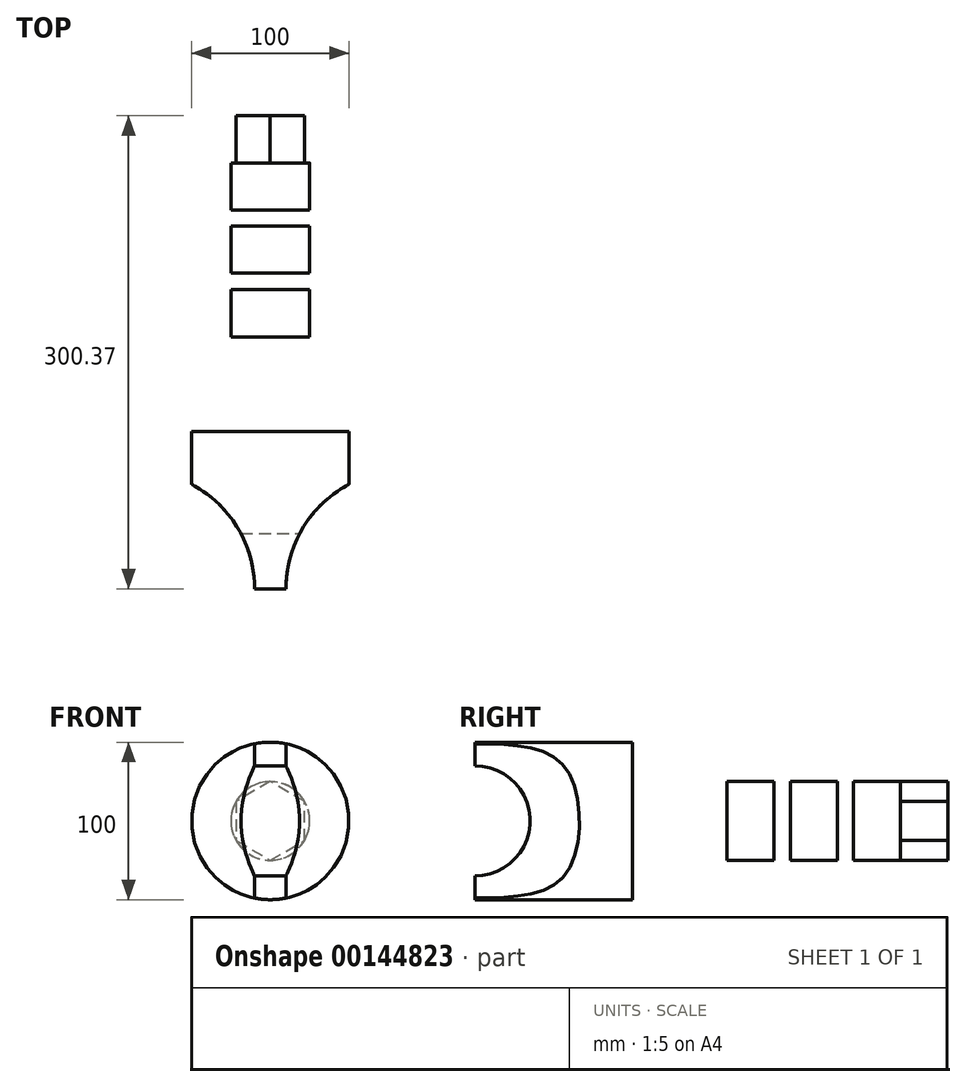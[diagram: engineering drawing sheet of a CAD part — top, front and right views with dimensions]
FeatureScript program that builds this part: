
annotation { "Feature Type Name" : "Feature", "Feature Type Description" : "" }
export const myFeature = defineFeature(function(context is Context, id is Id, definition is map)
    precondition{}
    {
        {
            var Q0;
            Q0=qCreatedBy(makeId("Top.planeOp"),FACE);
            var sketch = newSketch(context, id + "F0", { "sketchPlane" : qUnion([Q0])});
            skLineSegment(sketch, "E0", {"start": v(0, 0) * mm, "end": v(0, 300) * mm});
            skLineSegment(sketch, "E1.bottom", {"start": v(0, 0) * mm, "end": v(-50, 0) * mm});
            skLineSegment(sketch, "E1.top", {"start": v(0, 100) * mm, "end": v(-50, 100) * mm});
            skLineSegment(sketch, "E1.left", {"start": v(0, 0) * mm, "end": v(0, 100) * mm});
            skLineSegment(sketch, "E1.right", {"start": v(-50, 0) * mm, "end": v(-50, 100) * mm});
            skLineSegment(sketch, "E2.bottom", {"start": v(0, 100) * mm, "end": v(-25, 100) * mm});
            skLineSegment(sketch, "E2.top", {"start": v(0, 150) * mm, "end": v(-25, 150) * mm});
            skLineSegment(sketch, "E2.left", {"start": v(0, 100) * mm, "end": v(0, 150) * mm});
            skLineSegment(sketch, "E2.right", {"start": v(-25, 100) * mm, "end": v(-25, 150) * mm});
            skLineSegment(sketch, "E3.bottom", {"start": v(-12.5, 150) * mm, "end": v(0, 150) * mm});
            skLineSegment(sketch, "E3.top", {"start": v(-12.5, 160) * mm, "end": v(0, 160) * mm});
            skLineSegment(sketch, "E3.left", {"start": v(-12.5, 150) * mm, "end": v(-12.5, 160) * mm});
            skLineSegment(sketch, "E3.right", {"start": v(0, 150) * mm, "end": v(0, 160) * mm});
            skLineSegment(sketch, "E4.bottom", {"start": v(-25, 160) * mm, "end": v(0, 160) * mm});
            skLineSegment(sketch, "E4.top", {"start": v(-25, 190) * mm, "end": v(0, 190) * mm});
            skLineSegment(sketch, "E4.left", {"start": v(-25, 160) * mm, "end": v(-25, 190) * mm});
            skLineSegment(sketch, "E4.right", {"start": v(0, 160) * mm, "end": v(0, 190) * mm});
            skLineSegment(sketch, "E5.bottom", {"start": v(-12.5, 190) * mm, "end": v(0, 190) * mm});
            skLineSegment(sketch, "E5.top", {"start": v(-12.5, 200.37) * mm, "end": v(0, 200.37) * mm});
            skLineSegment(sketch, "E5.left", {"start": v(-12.5, 190) * mm, "end": v(-12.5, 200.37) * mm});
            skLineSegment(sketch, "E5.right", {"start": v(0, 190) * mm, "end": v(0, 200.37) * mm});
            skLineSegment(sketch, "E6.bottom", {"start": v(-25, 200.37) * mm, "end": v(0, 200.37) * mm});
            skLineSegment(sketch, "E6.top", {"start": v(-25, 230.37) * mm, "end": v(0, 230.37) * mm});
            skLineSegment(sketch, "E6.left", {"start": v(-25, 200.37) * mm, "end": v(-25, 230.37) * mm});
            skLineSegment(sketch, "E6.right", {"start": v(0, 200.37) * mm, "end": v(0, 230.37) * mm});
            skLineSegment(sketch, "E7.bottom", {"start": v(-12.5, 230.37) * mm, "end": v(0, 230.37) * mm});
            skLineSegment(sketch, "E7.top", {"start": v(-12.5, 240.37) * mm, "end": v(0, 240.37) * mm});
            skLineSegment(sketch, "E7.left", {"start": v(-12.5, 230.37) * mm, "end": v(-12.5, 240.37) * mm});
            skLineSegment(sketch, "E7.right", {"start": v(0, 230.37) * mm, "end": v(0, 240.37) * mm});
            skLineSegment(sketch, "E8.bottom", {"start": v(-25, 240.37) * mm, "end": v(0, 240.37) * mm});
            skLineSegment(sketch, "E8.top", {"start": v(-25, 270.37) * mm, "end": v(0, 270.37) * mm});
            skLineSegment(sketch, "E8.left", {"start": v(-25, 240.37) * mm, "end": v(-25, 270.37) * mm});
            skLineSegment(sketch, "E8.right", {"start": v(0, 240.37) * mm, "end": v(0, 270.37) * mm});
            skSolve(sketch);
        }
        {
            var Q0;
            Q0=makeQuery(id+"F0.imprint","IMPRINT",FACE,{"disambiguationData":[TD([[makeQuery(id+"F0.imprint","IMPRINT",EDGE,{"derivedFrom":sQuery(id+"F0.wireOp",EDGE,"E1.bottom")}),-1.0]])]});
            var Q1;
            Q1=makeQuery(id+"F0.imprint","IMPRINT",FACE,{"disambiguationData":[TD([[makeQuery(id+"F0.imprint","IMPRINT",EDGE,{"derivedFrom":sQuery(id+"F0.wireOp",EDGE,"E2.bottom")}),-1.0]])]});
            var Q2;
            Q2=makeQuery(id+"F0.imprint","IMPRINT",FACE,{"disambiguationData":[TD([[makeQuery(id+"F0.imprint","IMPRINT",EDGE,{"derivedFrom":sQuery(id+"F0.wireOp",EDGE,"E3.bottom")}),1.0]])]});
            var Q3;
            Q3=makeQuery(id+"F0.imprint","IMPRINT",FACE,{"disambiguationData":[TD([[makeQuery(id+"F0.imprint","IMPRINT",EDGE,{"derivedFrom":sQuery(id+"F0.wireOp",EDGE,"E4.top")}),-1.0]])]});
            var Q4;
            Q4=makeQuery(id+"F0.imprint","IMPRINT",FACE,{"disambiguationData":[TD([[makeQuery(id+"F0.imprint","IMPRINT",EDGE,{"derivedFrom":sQuery(id+"F0.wireOp",EDGE,"E5.bottom")}),1.0]])]});
            var Q5;
            Q5=makeQuery(id+"F0.imprint","IMPRINT",FACE,{"disambiguationData":[TD([[makeQuery(id+"F0.imprint","IMPRINT",EDGE,{"derivedFrom":sQuery(id+"F0.wireOp",EDGE,"E6.top")}),-1.0]])]});
            var Q6;
            Q6=makeQuery(id+"F0.imprint","IMPRINT",FACE,{"disambiguationData":[TD([[makeQuery(id+"F0.imprint","IMPRINT",EDGE,{"derivedFrom":sQuery(id+"F0.wireOp",EDGE,"E7.bottom")}),1.0]])]});
            var Q7;
            Q7=makeQuery(id+"F0.imprint","IMPRINT",FACE,{"disambiguationData":[TD([[makeQuery(id+"F0.imprint","IMPRINT",EDGE,{"derivedFrom":sQuery(id+"F0.wireOp",EDGE,"E8.top")}),-1.0]])]});
            var Q8;
            Q8=sQuery(id+"F0.wireOp",EDGE,"E0");
            revolve(context, id + "F1", {"entities" : qUnion([Q0, Q1, Q2, Q3, Q4, Q5, Q6, Q7]), "axis" : qUnion([Q8]), "revolveType" : RevolveType.FULL});
        }
        {
            var Q0;
            Q0=makeQuery(id+"F1.opRevolve","SWEPT_FACE",FACE,{"disambiguationData":[OSD([sQuery(id+"F0.wireOp",EDGE,"E8.top")])]});
            var sketch = newSketch(context, id + "F2", { "sketchPlane" : qUnion([Q0])});
            skCircle(sketch, "E9.cCircle", {"center": v(0, 0) * mm, "radius": 25 * mm, "construction": true});
            skLineSegment(sketch, "E9.0", {"start": v(0, -25) * mm, "end": v(-21.65, -12.5) * mm});
            skLineSegment(sketch, "E9.1", {"start": v(-21.65, -12.5) * mm, "end": v(-21.65, 12.5) * mm});
            skLineSegment(sketch, "E9.2", {"start": v(-21.65, 12.5) * mm, "end": v(0, 25) * mm});
            skLineSegment(sketch, "E9.3", {"start": v(0, 25) * mm, "end": v(21.65, 12.5) * mm});
            skLineSegment(sketch, "E9.4", {"start": v(21.65, 12.5) * mm, "end": v(21.65, -12.5) * mm});
            skLineSegment(sketch, "E9.5", {"start": v(21.65, -12.5) * mm, "end": v(0, -25) * mm});
            skSolve(sketch);
        }
        {
            var Q0;
            Q0=makeQuery(id+"F2.imprint","IMPRINT",FACE,{"disambiguationData":[TD([[makeQuery(id+"F2.imprint","IMPRINT",EDGE,{"derivedFrom":sQuery(id+"F2.wireOp",EDGE,"E9.0")}),-1.0]])]});
            extrude(context, id + "F3", {"entities" : qUnion([Q0]), "operationType" : NewBodyOperationType.ADD, "depth" : 30 * mm});
        }
        {
            var Q0;
            Q0=qCreatedBy(makeId("Right.planeOp"),FACE);
            cPlane(context, id + "F4", {"entities" : qUnion([Q0]), "cplaneType" : CPlaneType.OFFSET, "offset" : 50 * mm, "width" : 150 * mm, "height" : 150 * mm});
        }
        {
            var Q0;
            Q0=qCreatedBy(id+"F4.planeOp",FACE);
            var sketch = newSketch(context, id + "F5", { "sketchPlane" : qUnion([Q0])});
            skCircle(sketch, "E10", {"center": v(0, 0) * mm, "radius": 37.5 * mm});
            skSolve(sketch);
        }
        {
            var Q0;
            Q0=sQuery(id+"F5.wireOp",VERTEX,"E10.center");
            var Q1;
            Q1=makeQuery(id+"F1.opRevolve","SWEPT_BODY",BODY,{"disambiguationData":[OSD([sQuery(id+"F0.wireOp",EDGE,"E1.bottom"),sQuery(id+"F0.wireOp",EDGE,"E1.top"),sQuery(id+"F0.wireOp",EDGE,"E1.left"),sQuery(id+"F0.wireOp",EDGE,"E1.right"),sQuery(id+"F0.wireOp",EDGE,"E2.top"),sQuery(id+"F0.wireOp",EDGE,"E2.left"),sQuery(id+"F0.wireOp",EDGE,"E2.right"),sQuery(id+"F0.wireOp",EDGE,"E3.left"),sQuery(id+"F0.wireOp",EDGE,"E3.right"),sQuery(id+"F0.wireOp",EDGE,"E4.bottom"),sQuery(id+"F0.wireOp",EDGE,"E4.top"),sQuery(id+"F0.wireOp",EDGE,"E4.left"),sQuery(id+"F0.wireOp",EDGE,"E4.right"),sQuery(id+"F0.wireOp",EDGE,"E5.left"),sQuery(id+"F0.wireOp",EDGE,"E5.right"),sQuery(id+"F0.wireOp",EDGE,"E6.bottom"),sQuery(id+"F0.wireOp",EDGE,"E6.top"),sQuery(id+"F0.wireOp",EDGE,"E6.left"),sQuery(id+"F0.wireOp",EDGE,"E6.right"),sQuery(id+"F0.wireOp",EDGE,"E7.left"),sQuery(id+"F0.wireOp",EDGE,"E7.right"),sQuery(id+"F0.wireOp",EDGE,"E8.bottom"),sQuery(id+"F0.wireOp",EDGE,"E8.top"),sQuery(id+"F0.wireOp",EDGE,"E8.left"),sQuery(id+"F0.wireOp",EDGE,"E8.right")])]});
            hole(context, id + "F6", {"style" : HoleStyle.SIMPLE, "endStyle" : HoleEndStyle.THROUGH, "holeDiameter" : 70 * mm, "locations" : qUnion([Q0]), "scope" : qUnion([Q1]), "isTappedThrough" : true});
        }
        {
            var Q0;
            Q0=makeQuery(id+"F6.hole-0.boolean.opBoolean","SPLIT",FACE,{"disambiguationData":[OD(0.0)],"derivedFrom":makeQuery(id+"F1.opRevolve","SWEPT_FACE",FACE,{"disambiguationData":[OSD([sQuery(id+"F0.wireOp",EDGE,"E1.bottom")])]})});
            var sketch = newSketch(context, id + "F7", { "sketchPlane" : qUnion([Q0])});
            skLineSegment(sketch, "E11", {"start": v(0, 0) * mm, "end": v(10, 0) * mm});
            skLineSegment(sketch, "E12", {"start": v(10, 0) * mm, "end": v(-10, 0) * mm});
            skLineSegment(sketch, "E13.bottom", {"start": v(10, 50.79) * mm, "end": v(52.33, 50.79) * mm});
            skLineSegment(sketch, "E13.top", {"start": v(10, -53.13) * mm, "end": v(52.33, -53.13) * mm});
            skLineSegment(sketch, "E13.left", {"start": v(10, 50.79) * mm, "end": v(10, -53.13) * mm});
            skLineSegment(sketch, "E13.right", {"start": v(52.33, 50.79) * mm, "end": v(52.33, -53.13) * mm});
            skLineSegment(sketch, "E14.bottom", {"start": v(-10, 51.15) * mm, "end": v(-51.05, 51.15) * mm});
            skLineSegment(sketch, "E14.top", {"start": v(-10, -53.13) * mm, "end": v(-51.05, -53.13) * mm});
            skLineSegment(sketch, "E14.left", {"start": v(-10, 51.15) * mm, "end": v(-10, -53.13) * mm});
            skLineSegment(sketch, "E14.right", {"start": v(-51.05, 51.15) * mm, "end": v(-51.05, -53.13) * mm});
            skSolve(sketch);
        }
        {
            var Q0;
            {var subQ5=sQuery(id+"F7.wireOp",EDGE,"E13.bottom");Q0=makeQuery(id+"F7.imprint","IMPRINT",FACE,{"disambiguationData":[TD([[makeQuery(id+"F7.imprint","IMPRINT",EDGE,{"derivedFrom":subQ5}),-1.0]])]});}
            var Q1;
            {var subQ5=sQuery(id+"F7.wireOp",EDGE,"E14.bottom");Q1=makeQuery(id+"F7.imprint","IMPRINT",FACE,{"disambiguationData":[TD([[makeQuery(id+"F7.imprint","IMPRINT",EDGE,{"derivedFrom":subQ5}),1.0]])]});}
            var Q2;
            {var subQ0=sQuery(id+"F7.wireOp",EDGE,"E13.left");var subQ1=sQuery(id+"F0.wireOp",EDGE,"E1.bottom");var subQ2=makeQuery(id+"F6.hole-0.boolean.opBoolean","SPLIT",EDGE,{"disambiguationData":[OD(0.0)],"derivedFrom":makeQuery(id+"F1.opRevolve","SWEPT_EDGE",EDGE,{"disambiguationData":[OSD([subQ1,sQuery(id+"F0.wireOp",EDGE,"E1.right")])]})});var subQ3=makeQuery(id+"F7.imprint","INTERSECT",VERTEX,{"derivedFrom":[subQ2,subQ0]});Q2=makeQuery(id+"F7.imprint","IMPRINT",FACE,{"disambiguationData":[TD([[makeQuery(id+"F7.imprint","IMPRINT",EDGE,{"disambiguationData":[TD([[subQ3,1.0]])],"derivedFrom":subQ0}),1.0]])]});}
            var Q3;
            {var subQ0=sQuery(id+"F7.wireOp",EDGE,"E14.left");var subQ1=sQuery(id+"F0.wireOp",EDGE,"E1.bottom");var subQ2=makeQuery(id+"F6.hole-0.boolean.opBoolean","SPLIT",EDGE,{"disambiguationData":[OD(0.0)],"derivedFrom":makeQuery(id+"F1.opRevolve","SWEPT_EDGE",EDGE,{"disambiguationData":[OSD([subQ1,sQuery(id+"F0.wireOp",EDGE,"E1.right")])]})});var subQ3=makeQuery(id+"F7.imprint","INTERSECT",VERTEX,{"derivedFrom":[subQ2,subQ0]});Q3=makeQuery(id+"F7.imprint","IMPRINT",FACE,{"disambiguationData":[TD([[makeQuery(id+"F7.imprint","IMPRINT",EDGE,{"disambiguationData":[TD([[subQ3,1.0]])],"derivedFrom":subQ0}),-1.0]])]});}
            extrude(context, id + "F8", {"entities" : qUnion([Q0, Q1, Q2, Q3]), "operationType" : NewBodyOperationType.REMOVE, "oppositeDirection" : true, "depth" : 75 * mm});
        }
        {
            var Q0;
            Q0=makeQuery(id+"F8.boolean.opBoolean","COPY",EDGE,{"derivedFrom":makeQuery(id+"F8.opExtrude","CAP_EDGE",EDGE,{"disambiguationData":[OSD([sQuery(id+"F7.wireOp",EDGE,"E13.left")])],"isStart":false})});
            var Q1;
            Q1=makeQuery(id+"F8.boolean.opBoolean","COPY",EDGE,{"derivedFrom":makeQuery(id+"F8.opExtrude","CAP_EDGE",EDGE,{"disambiguationData":[OSD([sQuery(id+"F7.wireOp",EDGE,"E14.left")])],"isStart":false})});
            fillet(context, id + "F9", {"entities" : qUnion([Q0, Q1]), "radius" : 75 * mm, "tangentPropagation" : true, "allowEdgeOverflow" : false});
        }
    });
